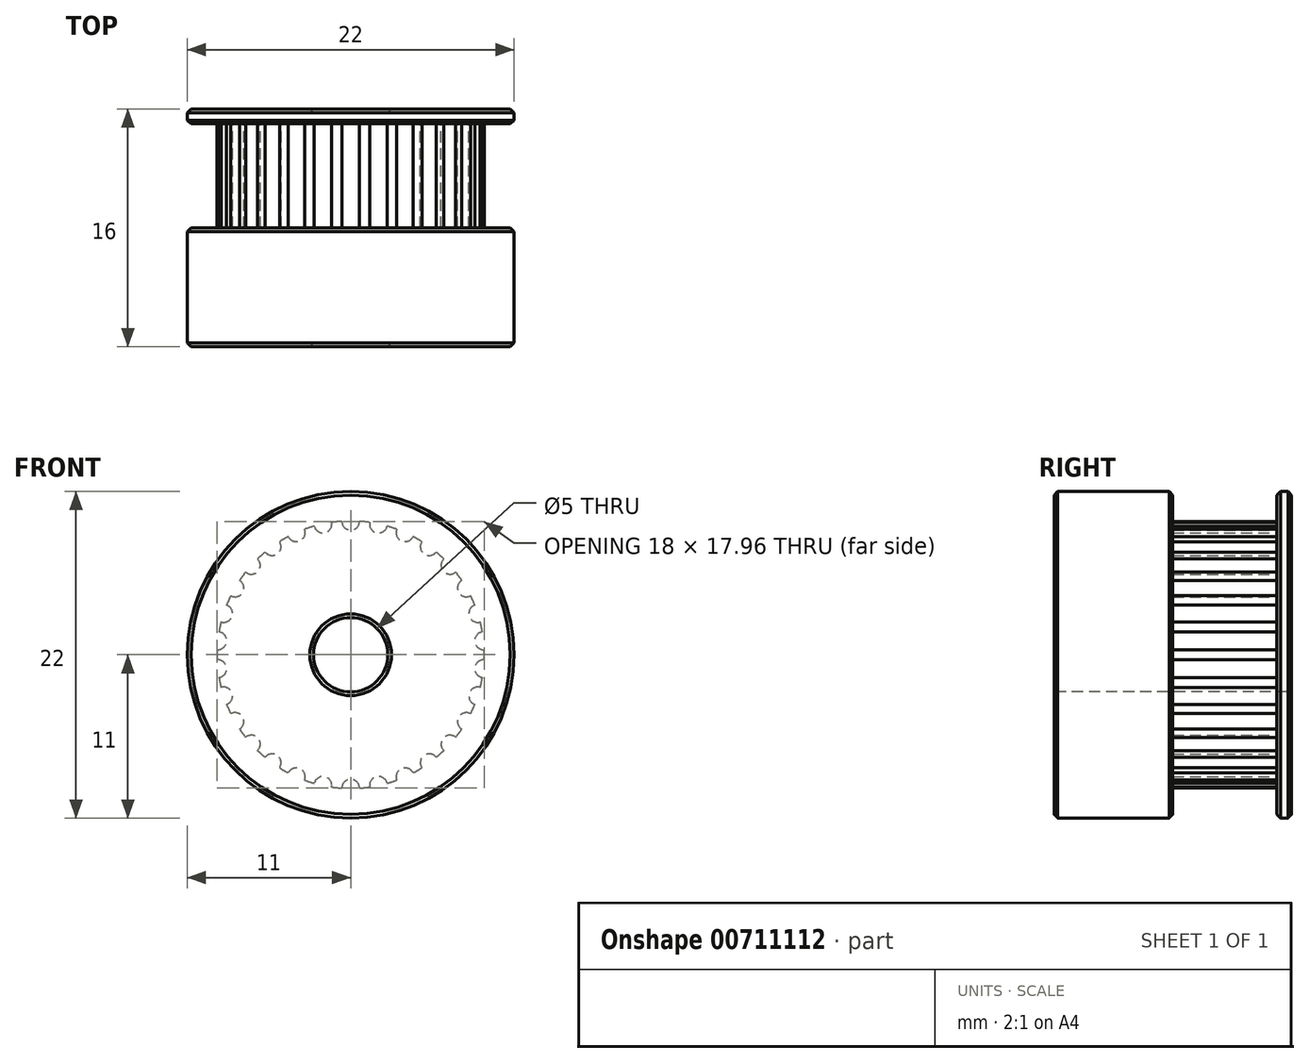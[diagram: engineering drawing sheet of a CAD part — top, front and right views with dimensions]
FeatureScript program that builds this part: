
annotation { "Feature Type Name" : "Feature", "Feature Type Description" : "" }
export const myFeature = defineFeature(function(context is Context, id is Id, definition is map)
    precondition{}
    {
        {
            var Q0;
            Q0=qCreatedBy(makeId("Front.planeOp"),FACE);
            var sketch = newSketch(context, id + "F0", { "sketchPlane" : qUnion([Q0])});
            skCircle(sketch, "E0", {"center": v(0, 0) * mm, "radius": 11 * mm});
            skSolve(sketch);
        }
        {
            var Q0;
            Q0=makeQuery(id+"F0.imprint","IMPRINT",FACE,{"disambiguationData":[TD([[makeQuery(id+"F0.imprint","IMPRINT",EDGE,{"derivedFrom":sQuery(id+"F0.wireOp",EDGE,"E0")}),1.0]])]});
            extrude(context, id + "F1", {"entities" : qUnion([Q0]), "depth" : 1 * mm, "offsetDistance" : 25 * mm});
        }
        {
            var Q0;
            Q0=makeQuery(id+"F1.opExtrude","CAP_FACE",FACE,{"disambiguationData":[OSD([sQuery(id+"F0.wireOp",EDGE,"E0")])],"isStart":false});
            var sketch = newSketch(context, id + "F2", { "sketchPlane" : qUnion([Q0])});
            skCircle(sketch, "E1", {"center": v(0, 0) * mm, "radius": 9 * mm});
            skSolve(sketch);
        }
        {
            var Q0;
            Q0=qSketchRegion(id+"F2",true);
            extrude(context, id + "F3", {"entities" : qUnion([Q0]), "operationType" : NewBodyOperationType.ADD, "depth" : 7 * mm, "offsetDistance" : 25 * mm});
        }
        {
            var Q0;
            Q0=makeQuery(id+"F3.opExtrude","CAP_FACE",FACE,{"disambiguationData":[OSD([sQuery(id+"F2.wireOp",EDGE,"E1")])],"isStart":false});
            var sketch = newSketch(context, id + "F4", { "sketchPlane" : qUnion([Q0])});
            skCircle(sketch, "E2", {"center": v(0, 0) * mm, "radius": 11 * mm});
            skSolve(sketch);
        }
        {
            var Q0;
            Q0=qSketchRegion(id+"F4",true);
            extrude(context, id + "F5", {"entities" : qUnion([Q0]), "operationType" : NewBodyOperationType.ADD, "depth" : 8 * mm, "offsetDistance" : 25 * mm});
        }
        {
            var Q0;
            Q0=makeQuery(id+"F1.opExtrude","CAP_FACE",FACE,{"disambiguationData":[OSD([sQuery(id+"F0.wireOp",EDGE,"E0")])],"isStart":false});
            var sketch = newSketch(context, id + "F6", { "sketchPlane" : qUnion([Q0])});
            skCircle(sketch, "E3", {"center": v(0, 0) * mm, "radius": 5 * mm, "construction": true});
            skLineSegment(sketch, "E4", {"start": v(-9, 0) * mm, "end": v(0, 0) * mm, "construction": true});
            skLineSegment(sketch, "E5", {"start": v(0, 0) * mm, "end": v(0, 9) * mm, "construction": true});
            skCircle(sketch, "E6", {"center": v(0, 9) * mm, "radius": 0.6 * mm});
            skCircle(sketch, "E7.1.0", {"center": v(-1.87, 8.8) * mm, "radius": 0.6 * mm});
            skCircle(sketch, "E7.2.0", {"center": v(-3.66, 8.22) * mm, "radius": 0.6 * mm});
            skCircle(sketch, "E7.3.0", {"center": v(-5.3, 7.28) * mm, "radius": 0.6 * mm});
            skCircle(sketch, "E7.4.0", {"center": v(-6.69, 6.02) * mm, "radius": 0.6 * mm});
            skCircle(sketch, "E7.5.0", {"center": v(-7.8, 4.5) * mm, "radius": 0.6 * mm});
            skCircle(sketch, "E7.6.0", {"center": v(-8.56, 2.78) * mm, "radius": 0.6 * mm});
            skCircle(sketch, "E7.7.0", {"center": v(-8.95, 0.94) * mm, "radius": 0.6 * mm});
            skCircle(sketch, "E7.8.0", {"center": v(-8.95, -0.94) * mm, "radius": 0.6 * mm});
            skCircle(sketch, "E7.9.0", {"center": v(-8.56, -2.78) * mm, "radius": 0.6 * mm});
            skCircle(sketch, "E7.10.0", {"center": v(-7.8, -4.5) * mm, "radius": 0.6 * mm});
            skCircle(sketch, "E7.11.0", {"center": v(-6.69, -6.02) * mm, "radius": 0.6 * mm});
            skCircle(sketch, "E7.12.0", {"center": v(-5.3, -7.28) * mm, "radius": 0.6 * mm});
            skCircle(sketch, "E7.13.0", {"center": v(-3.66, -8.22) * mm, "radius": 0.6 * mm});
            skCircle(sketch, "E7.14.0", {"center": v(-1.87, -8.8) * mm, "radius": 0.6 * mm});
            skCircle(sketch, "E7.15.0", {"center": v(0, -9) * mm, "radius": 0.6 * mm});
            skCircle(sketch, "E8.1.16.0", {"center": v(1.87, -8.8) * mm, "radius": 0.6 * mm});
            skCircle(sketch, "E8.1.17.0", {"center": v(3.66, -8.22) * mm, "radius": 0.6 * mm});
            skCircle(sketch, "E8.1.18.0", {"center": v(5.3, -7.28) * mm, "radius": 0.6 * mm});
            skCircle(sketch, "E8.1.19.0", {"center": v(6.69, -6.02) * mm, "radius": 0.6 * mm});
            skCircle(sketch, "E9.1.20.0", {"center": v(7.8, -4.5) * mm, "radius": 0.6 * mm});
            skCircle(sketch, "E9.1.21.0", {"center": v(8.56, -2.78) * mm, "radius": 0.6 * mm});
            skCircle(sketch, "E9.1.22.0", {"center": v(8.95, -0.94) * mm, "radius": 0.6 * mm});
            skCircle(sketch, "E9.1.23.0", {"center": v(8.95, 0.94) * mm, "radius": 0.6 * mm});
            skCircle(sketch, "E9.1.24.0", {"center": v(8.56, 2.78) * mm, "radius": 0.6 * mm});
            skCircle(sketch, "E9.1.25.0", {"center": v(7.8, 4.5) * mm, "radius": 0.6 * mm});
            skCircle(sketch, "E9.1.26.0", {"center": v(6.69, 6.02) * mm, "radius": 0.6 * mm});
            skCircle(sketch, "E9.1.27.0", {"center": v(5.3, 7.28) * mm, "radius": 0.6 * mm});
            skCircle(sketch, "E9.1.28.0", {"center": v(3.66, 8.22) * mm, "radius": 0.6 * mm});
            skCircle(sketch, "E9.1.29.0", {"center": v(1.87, 8.8) * mm, "radius": 0.6 * mm});
            skSolve(sketch);
        }
        {
            var Q0;
            Q0=qSketchRegion(id+"F6",true);
            var Q1;
            Q1=makeQuery(id+"F5.opExtrude","CAP_FACE",FACE,{"disambiguationData":[OSD([sQuery(id+"F4.wireOp",EDGE,"E2")])],"isStart":true});
            extrude(context, id + "F7", {"entities" : qUnion([Q0]), "operationType" : NewBodyOperationType.REMOVE, "endBound" : BoundingType.UP_TO_SURFACE, "depth" : 7.5 * mm, "endBoundEntityFace" : qUnion([Q1]), "offsetDistance" : 25 * mm});
        }
        {
            var Q0;
            Q0=makeQuery(id+"F5.opExtrude","CAP_FACE",FACE,{"disambiguationData":[OSD([sQuery(id+"F4.wireOp",EDGE,"E2")])],"isStart":false});
            var sketch = newSketch(context, id + "F8", { "sketchPlane" : qUnion([Q0])});
            skCircle(sketch, "E10", {"center": v(0, 0) * mm, "radius": 2.5 * mm});
            skSolve(sketch);
        }
        {
            var Q0;
            Q0=qSketchRegion(id+"F8",true);
            extrude(context, id + "F9", {"entities" : qUnion([Q0]), "operationType" : NewBodyOperationType.REMOVE, "endBound" : BoundingType.THROUGH_ALL, "oppositeDirection" : true, "depth" : 25 * mm, "offsetDistance" : 25 * mm});
        }
        {
            var Q0;
            Q0=makeQuery(id+"F5.opExtrude","SWEPT_FACE",FACE,{"disambiguationData":[OSD([sQuery(id+"F4.wireOp",EDGE,"E2")])]});
            var Q1;
            Q1=makeQuery(id+"F1.opExtrude","SWEPT_FACE",FACE,{"disambiguationData":[OSD([sQuery(id+"F0.wireOp",EDGE,"E0")])]});
            var Q2;
            Q2=makeQuery(id+"F9.boolean.opBoolean","COPY",FACE,{"derivedFrom":makeQuery(id+"F9.opExtrude","SWEPT_FACE",FACE,{"disambiguationData":[OSD([sQuery(id+"F8.wireOp",EDGE,"E10")])]})});
            chamfer(context, id + "F10", {"entities" : qUnion([Q0, Q1, Q2]), "width" : 0.25 * mm, "tangentPropagation" : true});
        }
    });
